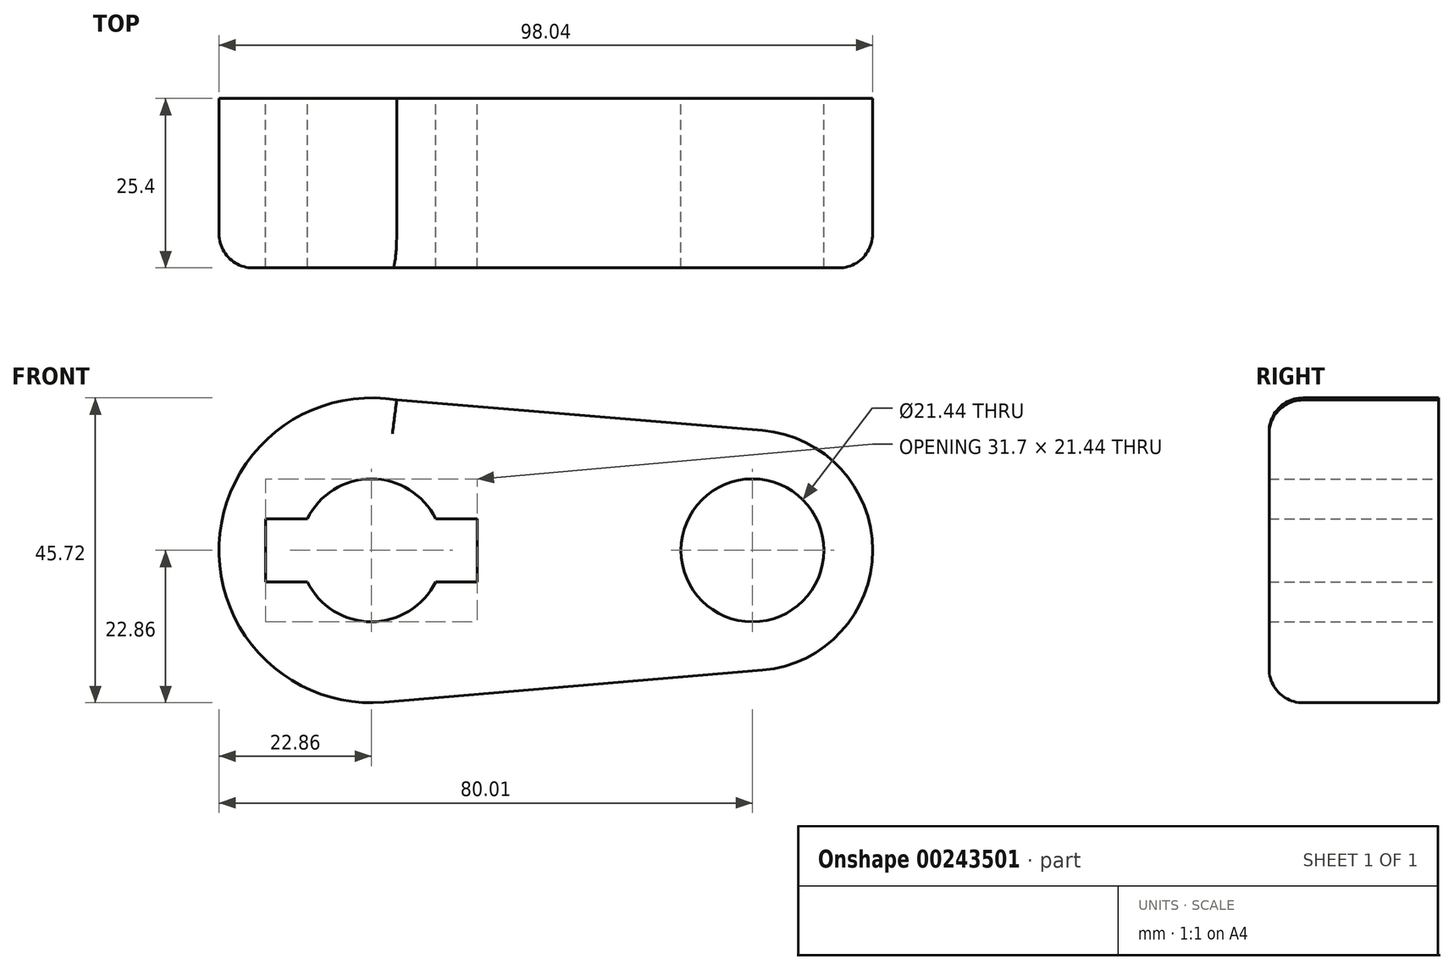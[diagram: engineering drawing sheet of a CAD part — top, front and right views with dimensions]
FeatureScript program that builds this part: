
annotation { "Feature Type Name" : "Feature", "Feature Type Description" : "" }
export const myFeature = defineFeature(function(context is Context, id is Id, definition is map)
    precondition{}
    {
        {
            var Q0;
            Q0=qCreatedBy(makeId("Front.planeOp"),FACE);
            var sketch = newSketch(context, id + "F0", { "sketchPlane" : qUnion([Q0])});
            skCircle(sketch, "E0", {"center": v(0, 0) * mm, "radius": 22.86 * mm});
            skCircle(sketch, "E1", {"center": v(57.15, 0) * mm, "radius": 18.03 * mm});
            skLineSegment(sketch, "E2", {"start": v(1.93, -22.78) * mm, "end": v(58.67, -17.97) * mm});
            skLineSegment(sketch, "E3", {"start": v(0, 22.86) * mm, "end": v(58.65, 17.97) * mm});
            skCircle(sketch, "E4", {"center": v(0, 0) * mm, "radius": 10.72 * mm});
            skCircle(sketch, "E5", {"center": v(57.15, 0) * mm, "radius": 10.72 * mm});
            skLineSegment(sketch, "E6.bottom", {"start": v(-15.85, 4.72) * mm, "end": v(15.85, 4.72) * mm});
            skLineSegment(sketch, "E6.top", {"start": v(-15.85, -4.72) * mm, "end": v(15.85, -4.72) * mm});
            skLineSegment(sketch, "E6.left", {"start": v(-15.85, 4.72) * mm, "end": v(-15.85, -4.72) * mm});
            skLineSegment(sketch, "E6.right", {"start": v(15.85, 4.72) * mm, "end": v(15.85, -4.72) * mm});
            skSolve(sketch);
        }
        {
            var Q0;
            Q0 = qSketchRegion(id + "F0", true);
            extrude(context, id + "F1", {"entities" : qUnion([Q0]), "depth" : 25.4 * mm});
        }
        {
            var Q0;
            Q0=makeQuery(id+"F1.opExtrude","CAP_EDGE",EDGE,{"disambiguationData":[OSD([sQuery(id+"F0.wireOp",EDGE,"E0")])],"isStart":false});
            var Q1;
            Q1=makeQuery(id+"F1.opExtrude","CAP_EDGE",EDGE,{"disambiguationData":[OSD([sQuery(id+"F0.wireOp",EDGE,"E3")])],"isStart":false});
            var Q2;
            Q2=makeQuery(id+"F1.opExtrude","CAP_EDGE",EDGE,{"disambiguationData":[OSD([sQuery(id+"F0.wireOp",EDGE,"E1")])],"isStart":false});
            var Q3;
            Q3=makeQuery(id+"F1.opExtrude","CAP_EDGE",EDGE,{"disambiguationData":[OSD([sQuery(id+"F0.wireOp",EDGE,"E2")])],"isStart":false});
            fillet(context, id + "F2", {"entities" : qUnion([Q0, Q1, Q2, Q3]), "radius" : 5.08 * mm, "tangentPropagation" : true, "allowEdgeOverflow" : false});
        }
    });
